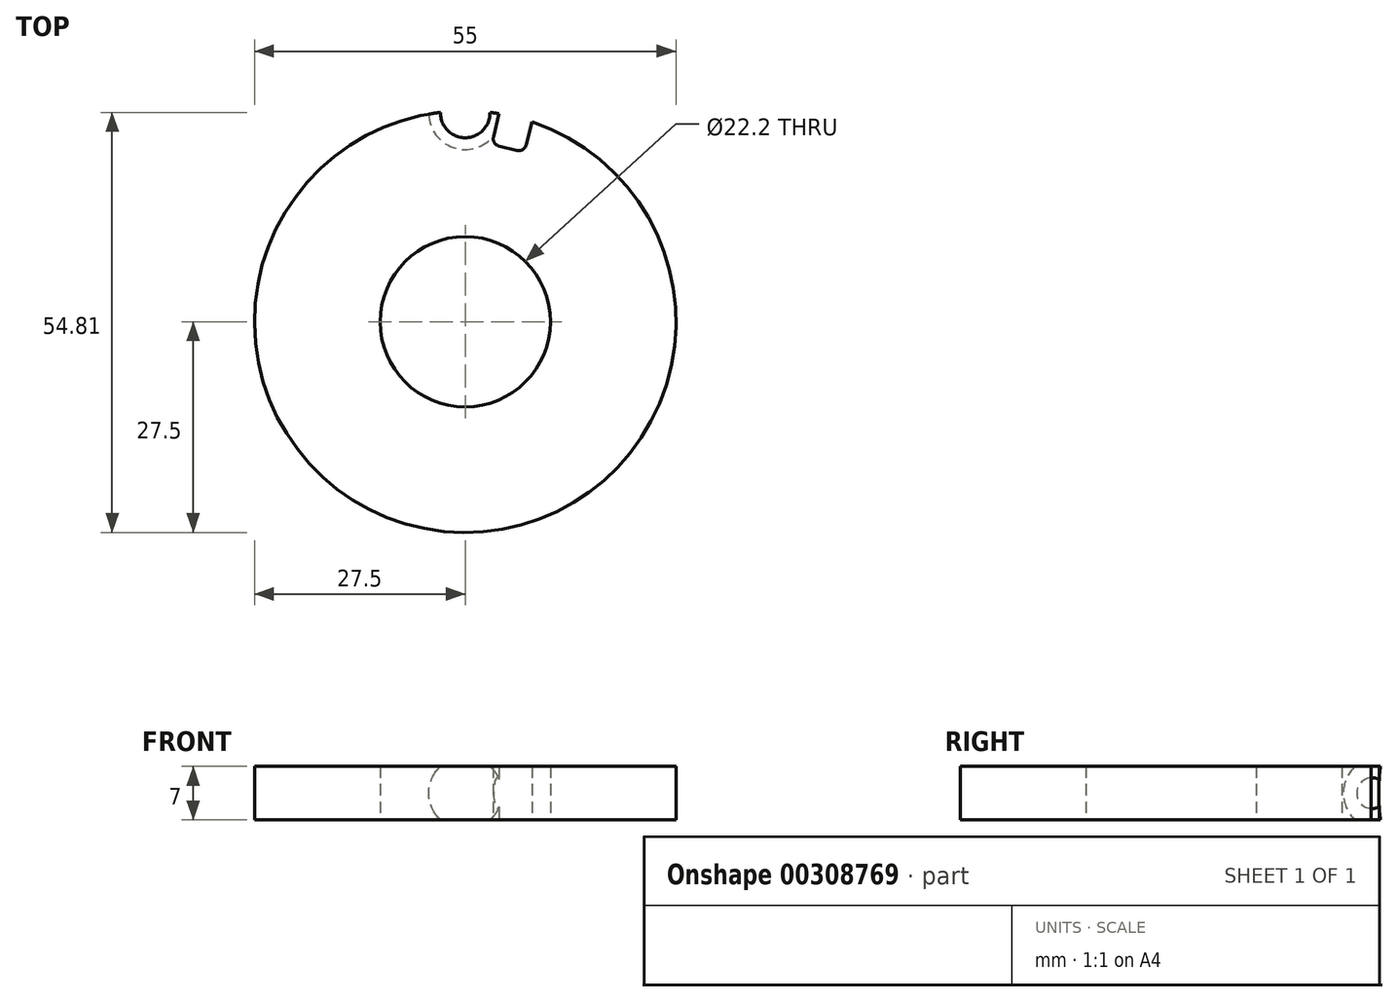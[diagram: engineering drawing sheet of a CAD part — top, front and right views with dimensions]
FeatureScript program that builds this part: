
annotation { "Feature Type Name" : "Feature", "Feature Type Description" : "" }
export const myFeature = defineFeature(function(context is Context, id is Id, definition is map)
    precondition{}
    {
        {
            var Q0;
            Q0=qCreatedBy(makeId("Top.planeOp"),FACE);
            var sketch = newSketch(context, id + "F0", { "sketchPlane" : qUnion([Q0])});
            skCircle(sketch, "E0", {"center": v(0, 0) * mm, "radius": 11.1 * mm});
            skCircle(sketch, "E1", {"center": v(0, 0) * mm, "radius": 27.5 * mm});
            skSolve(sketch);
        }
        {
            var Q0;
            Q0=makeQuery(id+"F0.imprint","IMPRINT",FACE,{"disambiguationData":[TD([[makeQuery(id+"F0.imprint","IMPRINT",EDGE,{"derivedFrom":sQuery(id+"F0.wireOp",EDGE,"E0")}),-1.0]])]});
            extrude(context, id + "F1", {"entities" : qUnion([Q0]), "depth" : 7 * mm});
        }
        {
            var Q0;
            Q0=qCreatedBy(makeId("Top.planeOp"),FACE);
            cPlane(context, id + "F2", {"entities" : qUnion([Q0]), "cplaneType" : CPlaneType.OFFSET, "offset" : 7 * mm / 2, "width" : 150 * mm, "height" : 150 * mm});
        }
        {
            var Q0;
            Q0=qCreatedBy(id+"F2.planeOp",FACE);
            var sketch = newSketch(context, id + "F3", { "sketchPlane" : qUnion([Q0])});
            skLineSegment(sketch, "E2", {"start": v(0, 0) * mm, "end": v(0, 81.99) * mm, "construction": true});
            skLineSegment(sketch, "E3", {"start": v(0, 27.23) * mm, "end": v(-4.76, 27.23) * mm});
            skLineSegment(sketch, "E4", {"start": v(0, 27.23) * mm, "end": v(4.76, 27.23) * mm});
            skArc(sketch, "E5", {"start": v(-4.76, 27.23) * mm, "mid": v(0, 32) * mm, "end": v(4.76, 27.23) * mm});
            skSolve(sketch);
        }
        {
            var Q0;
            Q0=makeQuery(id+"F3.imprint","IMPRINT",FACE,{"disambiguationData":[TD([[makeQuery(id+"F3.imprint","IMPRINT",EDGE,{"derivedFrom":sQuery(id+"F3.wireOp",EDGE,"E3")}),-1.0]])]});
            var Q1;
            Q1=sQuery(id+"F3.wireOp",EDGE,"E4");
            revolve(context, id + "F4", {"operationType" : NewBodyOperationType.REMOVE, "entities" : qUnion([Q0]), "axis" : qUnion([Q1]), "revolveType" : RevolveType.FULL});
        }
        {
            var Q0;
            Q0=qCreatedBy(makeId("Front.planeOp"),FACE);
            var sketch = newSketch(context, id + "F5", { "sketchPlane" : qUnion([Q0])});
            skLineSegment(sketch, "E6", {"start": v(0, 0) * mm, "end": v(0, 17.17) * mm, "construction": true});
            skSolve(sketch);
        }
        {
            var Q0;
            Q0=qCreatedBy(id+"F2.planeOp",FACE);
            var sketch = newSketch(context, id + "F6", { "sketchPlane" : qUnion([Q0])});
            skPoint(sketch, "E7.0", {"position": v(0, 24) * mm});
            skPoint(sketch, "E8.0", {"position": v(11.15, 21.25) * mm});
            skLineSegment(sketch, "E9", {"start": v(4.4, 22.92) * mm, "end": v(6.75, 22.34) * mm, "construction": true});
            skLineSegment(sketch, "E10", {"start": v(5.58, 22.63) * mm, "end": v(6.8, 27.62) * mm, "construction": true});
            skArc(sketch, "E11.0", {"start": v(-3.23, 27.3) * mm, "mid": v(0, 24) * mm, "end": v(3.23, 27.3) * mm});
            skLineSegment(sketch, "E12", {"start": v(3.23, 27.3) * mm, "end": v(2.28, 23.44) * mm, "construction": true});
            skLineSegment(sketch, "E13.bottom", {"start": v(8.81, 26.56) * mm, "end": v(4.54, 27.61) * mm});
            skLineSegment(sketch, "E13.top", {"start": v(7.72, 22.1) * mm, "end": v(3.44, 23.16) * mm});
            skLineSegment(sketch, "E13.left", {"start": v(8.81, 26.56) * mm, "end": v(7.96, 23.07) * mm});
            skLineSegment(sketch, "E13.right", {"start": v(4.54, 27.61) * mm, "end": v(3.68, 24.13) * mm});
            skPoint(sketch, "E13.middle", {"position": v(6.13, 24.86) * mm});
            skArc(sketch, "E14.filletArc", {"start": v(3.68, 24.13) * mm, "mid": v(3.8, 23.37) * mm, "end": v(4.4, 22.92) * mm});
            skArc(sketch, "E15.filletArc", {"start": v(6.75, 22.34) * mm, "mid": v(7.5, 22.46) * mm, "end": v(7.96, 23.07) * mm});
            skSolve(sketch);
        }
        {
            var Q0;
            Q0=makeQuery(id+"F6.imprint","IMPRINT",FACE,{"disambiguationData":[TD([[makeQuery(id+"F6.imprint","IMPRINT",EDGE,{"derivedFrom":sQuery(id+"F6.wireOp",EDGE,"E13.bottom")}),1.0]])]});
            extrude(context, id + "F7", {"entities" : qUnion([Q0]), "operationType" : NewBodyOperationType.REMOVE, "endBound" : BoundingType.SYMMETRIC, "depth" : 10 * mm});
        }
    });
